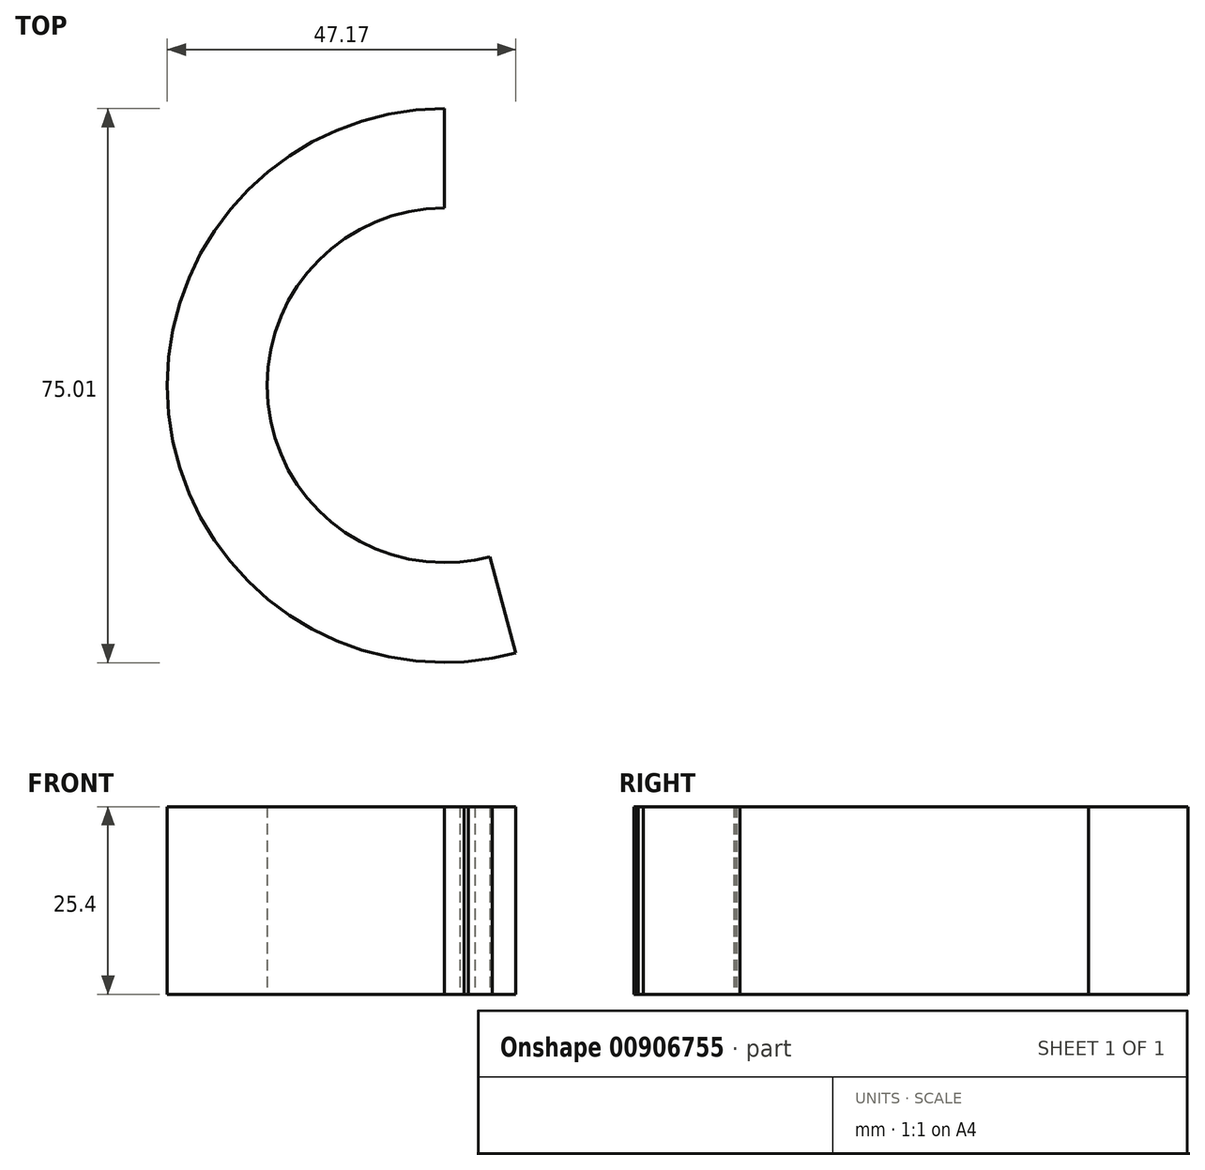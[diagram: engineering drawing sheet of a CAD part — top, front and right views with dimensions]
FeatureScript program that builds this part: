
annotation { "Feature Type Name" : "Feature", "Feature Type Description" : "" }
export const myFeature = defineFeature(function(context is Context, id is Id, definition is map)
    precondition{}
    {
        {
            var Q0;
            Q0=qCreatedBy(makeId("Top.planeOp"),FACE);
            var sketch = newSketch(context, id + "F0", { "sketchPlane" : qUnion([Q0])});
            skArc(sketch, "E0", {"start": v(0, 37.5) * mm, "mid": v(-37.5, 0) * mm, "end": v(0, -37.5) * mm});
            skLineSegment(sketch, "E1", {"start": v(0, 37.5) * mm, "end": v(0, 24.02) * mm});
            skArc(sketch, "E2", {"start": v(0, 24.02) * mm, "mid": v(-24, 0.03) * mm, "end": v(0, -23.97) * mm});
            skLineSegment(sketch, "E3", {"start": v(0, -23.97) * mm, "end": v(2.08, -23.88) * mm});
            skLineSegment(sketch, "E4", {"start": v(2.66, -37.4) * mm, "end": v(0, -37.5) * mm});
            skLineSegment(sketch, "E5", {"start": v(2.08, -23.88) * mm, "end": v(4.15, -23.61) * mm});
            skLineSegment(sketch, "E6", {"start": v(4.15, -23.61) * mm, "end": v(6.2, -23.17) * mm});
            skLineSegment(sketch, "E7", {"start": v(6.2, -23.17) * mm, "end": v(9.67, -36.22) * mm});
            skLineSegment(sketch, "E8", {"start": v(9.67, -36.22) * mm, "end": v(6.5, -36.93) * mm});
            skLineSegment(sketch, "E9", {"start": v(6.5, -36.93) * mm, "end": v(3.28, -37.35) * mm});
            skLineSegment(sketch, "E10", {"start": v(3.28, -37.35) * mm, "end": v(2.66, -37.4) * mm});
            skSolve(sketch);
        }
        {
            var Q0;
            Q0 = qSketchRegion(id + "F0", true);
            extrude(context, id + "F1", {"entities" : qUnion([Q0]), "depth" : 25.4 * mm, "offsetDistance" : 25.4 * mm});
        }
    });
